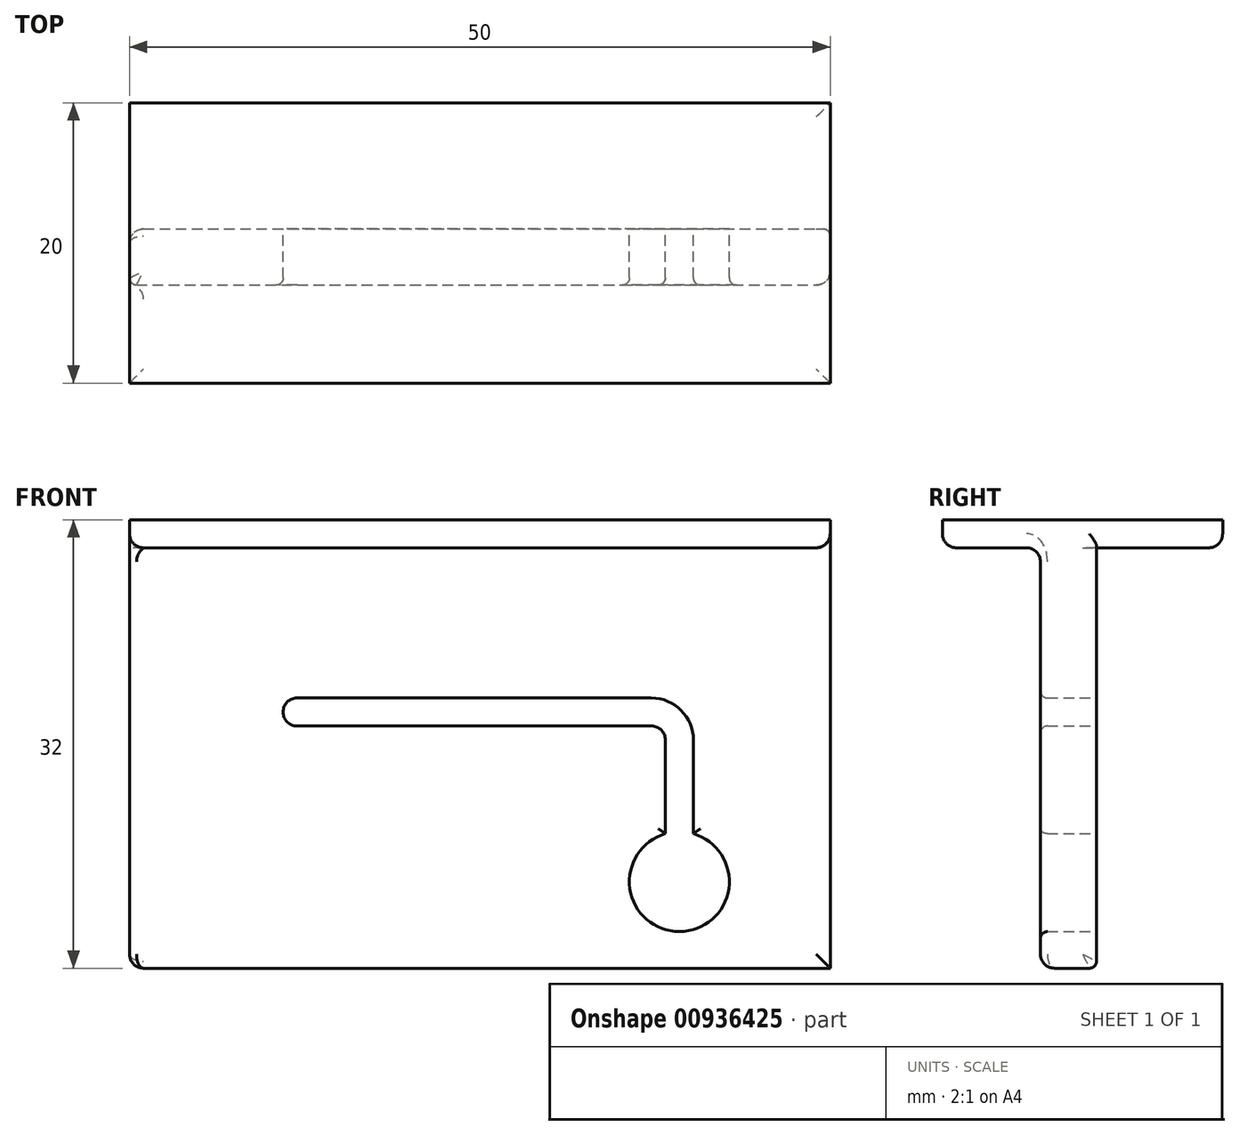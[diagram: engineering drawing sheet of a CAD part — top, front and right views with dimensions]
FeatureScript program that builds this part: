
annotation { "Feature Type Name" : "Feature", "Feature Type Description" : "" }
export const myFeature = defineFeature(function(context is Context, id is Id, definition is map)
    precondition{}
    {
        {
            var Q0;
            Q0=qCreatedBy(makeId("Front.planeOp"),FACE);
            var sketch = newSketch(context, id + "F0", { "sketchPlane" : qUnion([Q0])});
            skLineSegment(sketch, "E0.bottom", {"start": v(-25, 15) * mm, "end": v(25, 15) * mm});
            skLineSegment(sketch, "E0.top", {"start": v(-25, -15) * mm, "end": v(25, -15) * mm});
            skLineSegment(sketch, "E0.left", {"start": v(-25, 15) * mm, "end": v(-25, -15) * mm});
            skLineSegment(sketch, "E0.right", {"start": v(25, 15) * mm, "end": v(25, -15) * mm});
            skPoint(sketch, "E0.middle", {"position": v(0, 0) * mm});
            skSolve(sketch);
        }
        {
            var Q0;
            Q0 = qSketchRegion(id + "F0", true);
            extrude(context, id + "F1", {"entities" : qUnion([Q0]), "depth" : 4 * mm, "offsetDistance" : 25 * mm});
        }
        {
            var Q0;
            Q0=makeQuery(id+"F1.opExtrude","CAP_FACE",FACE,{"disambiguationData":[OSD([sQuery(id+"F0.wireOp",EDGE,"E0.bottom"),sQuery(id+"F0.wireOp",EDGE,"E0.top"),sQuery(id+"F0.wireOp",EDGE,"E0.left"),sQuery(id+"F0.wireOp",EDGE,"E0.right")])],"isStart":true});
            var sketch = newSketch(context, id + "F2", { "sketchPlane" : qUnion([Q0])});
            skLineSegment(sketch, "E1", {"start": v(-15.23, -5.4) * mm, "end": v(-15.23, 1.28) * mm});
            skLineSegment(sketch, "E2.0", {"start": v(-12.23, 2.28) * mm, "end": v(13.04, 2.28) * mm});
            skLineSegment(sketch, "E3.0", {"start": v(-12.23, 4.28) * mm, "end": v(13.04, 4.28) * mm});
            skLineSegment(sketch, "E4.0", {"start": v(-13.23, -5.4) * mm, "end": v(-13.23, 1.28) * mm});
            skLineSegment(sketch, "E5", {"start": v(-14.23, 0) * mm, "end": v(-14.23, -8.82) * mm, "construction": true});
            skArc(sketch, "E6", {"start": v(-15.23, -5.4) * mm, "mid": v(-14.23, -12.39) * mm, "end": v(-13.23, -5.4) * mm});
            skPoint(sketch, "E7.visualSharp", {"position": v(-13.23, 2.28) * mm});
            skArc(sketch, "E7.filletArc", {"start": v(-12.23, 2.28) * mm, "mid": v(-12.94, 2) * mm, "end": v(-13.23, 1.28) * mm});
            skLineSegment(sketch, "E8", {"start": v(13.04, 4.28) * mm, "end": v(13.04, 2.28) * mm, "construction": true});
            skArc(sketch, "E9", {"start": v(13.04, 2.28) * mm, "mid": v(14.04, 3.28) * mm, "end": v(13.04, 4.28) * mm});
            skArc(sketch, "E10.0", {"start": v(-12.23, 4.28) * mm, "mid": v(-14.35, 3.4) * mm, "end": v(-15.23, 1.28) * mm});
            skSolve(sketch);
        }
        {
            var Q0;
            Q0 = qSketchRegion(id + "F2", true);
            extrude(context, id + "F3", {"entities" : qUnion([Q0]), "operationType" : NewBodyOperationType.REMOVE, "oppositeDirection" : true, "depth" : 25 * mm, "offsetDistance" : 25 * mm});
        }
        {
            var Q0;
            Q0=makeQuery(id+"F1.opExtrude","SWEPT_FACE",FACE,{"disambiguationData":[OSD([sQuery(id+"F0.wireOp",EDGE,"E0.bottom")])]});
            var sketch = newSketch(context, id + "F4", { "sketchPlane" : qUnion([Q0])});
            skLineSegment(sketch, "E11.bottom", {"start": v(25, -11) * mm, "end": v(-25, -11) * mm});
            skLineSegment(sketch, "E11.top", {"start": v(25, 9) * mm, "end": v(-25, 9) * mm});
            skLineSegment(sketch, "E11.left", {"start": v(25, -11) * mm, "end": v(25, 9) * mm});
            skLineSegment(sketch, "E11.right", {"start": v(-25, -11) * mm, "end": v(-25, 9) * mm});
            skPoint(sketch, "E11.middle", {"position": v(0, -1) * mm});
            skSolve(sketch);
        }
        {
            var Q0;
            Q0 = qSketchRegion(id + "F4", true);
            extrude(context, id + "F5", {"entities" : qUnion([Q0]), "operationType" : NewBodyOperationType.ADD, "depth" : 2 * mm, "offsetDistance" : 25 * mm});
        }
        {
            var Q0;
            Q0=makeQuery(id+"F3.boolean.opBoolean","INTERSECT",EDGE,{"derivedFrom":[makeQuery(id+"F1.opExtrude","CAP_FACE",FACE,{"disambiguationData":[OSD([sQuery(id+"F0.wireOp",EDGE,"E0.bottom"),sQuery(id+"F0.wireOp",EDGE,"E0.top"),sQuery(id+"F0.wireOp",EDGE,"E0.left"),sQuery(id+"F0.wireOp",EDGE,"E0.right")])],"isStart":false}),makeQuery(id+"F3.opExtrude","SWEPT_FACE",FACE,{"disambiguationData":[OSD([sQuery(id+"F2.wireOp",EDGE,"E2.0")])]})]});
            var Q1;
            Q1=makeQuery(id+"F3.boolean.opBoolean","INTERSECT",EDGE,{"derivedFrom":[makeQuery(id+"F1.opExtrude","CAP_FACE",FACE,{"disambiguationData":[OSD([sQuery(id+"F0.wireOp",EDGE,"E0.bottom"),sQuery(id+"F0.wireOp",EDGE,"E0.top"),sQuery(id+"F0.wireOp",EDGE,"E0.left"),sQuery(id+"F0.wireOp",EDGE,"E0.right")])],"isStart":false}),makeQuery(id+"F3.opExtrude","SWEPT_FACE",FACE,{"disambiguationData":[OSD([sQuery(id+"F2.wireOp",EDGE,"E6")])]})]});
            var Q2;
            Q2=makeQuery(id+"F3.boolean.opBoolean","COPY",EDGE,{"derivedFrom":makeQuery(id+"F3.opExtrude","CAP_EDGE",EDGE,{"disambiguationData":[OSD([sQuery(id+"F2.wireOp",EDGE,"E2.0")])],"isStart":true})});
            var Q3;
            Q3=makeQuery(id+"F3.boolean.opBoolean","COPY",EDGE,{"derivedFrom":makeQuery(id+"F3.opExtrude","CAP_EDGE",EDGE,{"disambiguationData":[OSD([sQuery(id+"F2.wireOp",EDGE,"E6")])],"isStart":true})});
            var Q4;
            Q4=makeQuery(id+"F1.opExtrude","CAP_EDGE",EDGE,{"disambiguationData":[OSD([sQuery(id+"F0.wireOp",EDGE,"E0.left")])],"isStart":false});
            var Q5;
            Q5=makeQuery(id+"F1.opExtrude","CAP_EDGE",EDGE,{"disambiguationData":[OSD([sQuery(id+"F0.wireOp",EDGE,"E0.top")])],"isStart":true});
            var Q6;
            Q6=makeQuery(id+"F1.opExtrude","CAP_EDGE",EDGE,{"disambiguationData":[OSD([sQuery(id+"F0.wireOp",EDGE,"E0.right")])],"isStart":true});
            fillet(context, id + "F6", {"entities" : qUnion([Q0, Q1, Q2, Q3, Q4, Q5, Q6]), "radius" : .5 * mm, "tangentPropagation" : true, "allowEdgeOverflow" : false});
        }
        {
            var Q0;
            Q0=makeQuery(id+"F1.opExtrude","CAP_FACE",FACE,{"disambiguationData":[OSD([sQuery(id+"F0.wireOp",EDGE,"E0.bottom"),sQuery(id+"F0.wireOp",EDGE,"E0.top"),sQuery(id+"F0.wireOp",EDGE,"E0.left"),sQuery(id+"F0.wireOp",EDGE,"E0.right")])],"isStart":false});
            var Q1;
            {var subQ2=sQuery(id+"F4.wireOp",EDGE,"E11.bottom");var subQ3=sQuery(id+"F4.wireOp",EDGE,"E11.left");var subQ4=sQuery(id+"F4.wireOp",EDGE,"E11.right");Q1=makeQuery(id+"F5.boolean.opBoolean","SPLIT",FACE,{"disambiguationData":[TD([makeQuery(id+"F5.opExtrude","SWEPT_FACE",FACE,{"disambiguationData":[OSD([subQ2])]})])],"derivedFrom":makeQuery(id+"F5.opExtrude","CAP_FACE",FACE,{"disambiguationData":[OSD([subQ2,sQuery(id+"F4.wireOp",EDGE,"E11.top"),subQ3,subQ4])],"isStart":true})});}
            var Q2;
            Q2=makeQuery(id+"F1.opExtrude","CAP_EDGE",EDGE,{"disambiguationData":[OSD([sQuery(id+"F0.wireOp",EDGE,"E0.bottom")])],"isStart":true});
            var Q3;
            {var subQ0=sQuery(id+"F4.wireOp",EDGE,"E11.left");var subQ1=sQuery(id+"F4.wireOp",EDGE,"E11.top");Q3=makeQuery(id+"F5.boolean.opBoolean","SPLIT",EDGE,{"disambiguationData":[TD([makeQuery(id+"F5.opExtrude","SWEPT_FACE",FACE,{"disambiguationData":[OSD([subQ1])]})])],"derivedFrom":makeQuery(id+"F5.opExtrude","CAP_EDGE",EDGE,{"disambiguationData":[OSD([subQ0])],"isStart":true})});}
            var Q4;
            Q4=makeQuery(id+"F5.opExtrude","CAP_EDGE",EDGE,{"disambiguationData":[OSD([sQuery(id+"F4.wireOp",EDGE,"E11.top")])],"isStart":true});
            fillet(context, id + "F7", {"entities" : qUnion([Q0, Q1, Q2, Q3, Q4]), "radius" : 1 * mm, "tangentPropagation" : true, "allowEdgeOverflow" : false});
        }
    });
